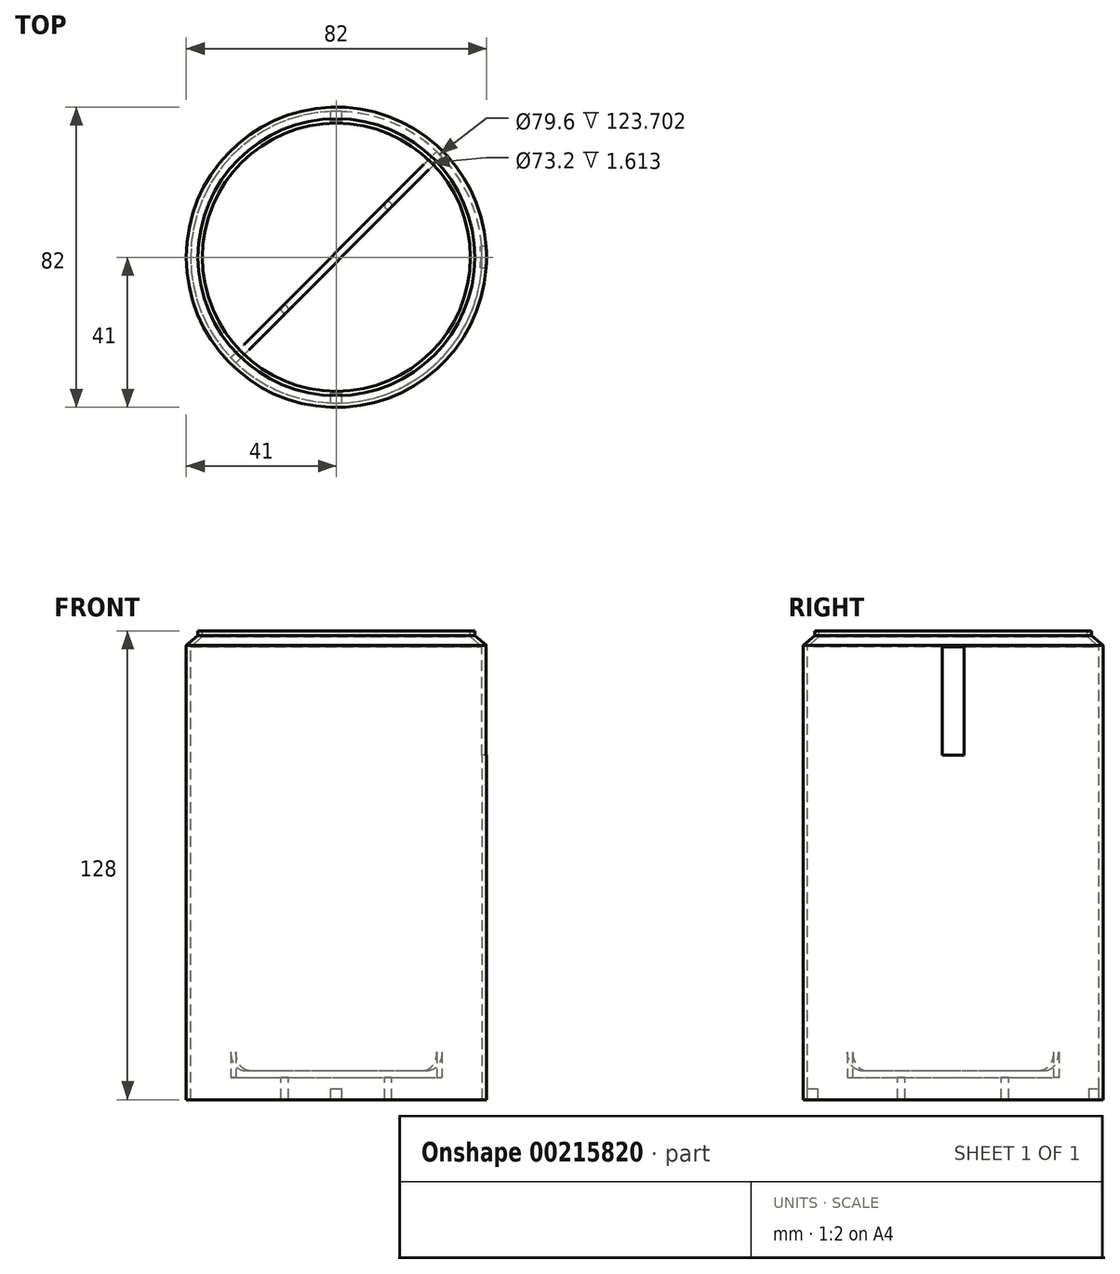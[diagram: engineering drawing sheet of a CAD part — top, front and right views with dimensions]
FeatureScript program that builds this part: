
annotation { "Feature Type Name" : "Feature", "Feature Type Description" : "" }
export const myFeature = defineFeature(function(context is Context, id is Id, definition is map)
    precondition{}
    {
        {
            var Q0;
            Q0=qCreatedBy(makeId("Right.planeOp"),FACE);
            var sketch = newSketch(context, id + "F0", { "sketchPlane" : qUnion([Q0])});
            skLineSegment(sketch, "E0", {"start": v(-41, 0) * mm, "end": v(-41, 124) * mm});
            skLineSegment(sketch, "E1", {"start": v(-39.8, 123.7) * mm, "end": v(-39.8, 0) * mm});
            skLineSegment(sketch, "E2", {"start": v(-39.8, 0) * mm, "end": v(-41, 0) * mm});
            skLineSegment(sketch, "E3", {"start": v(0, 64.87) * mm, "end": v(0, 0) * mm, "construction": true});
            skLineSegment(sketch, "E4", {"start": v(-37.8, 128) * mm, "end": v(-36.6, 128) * mm});
            skLineSegment(sketch, "E5", {"start": v(-37.8, 128) * mm, "end": v(-37.8, 126.69) * mm});
            skLineSegment(sketch, "E6", {"start": v(-36.6, 128) * mm, "end": v(-36.6, 126.39) * mm});
            skLineSegment(sketch, "E7", {"start": v(-37.8, 126.69) * mm, "end": v(-41, 124) * mm});
            skLineSegment(sketch, "E8", {"start": v(-36.6, 126.39) * mm, "end": v(-39.8, 123.7) * mm});
            skSolve(sketch);
        }
        {
            var Q0;
            Q0=qSketchRegion(id+"F0",true);
            var Q1;
            Q1=sQuery(id+"F0.wireOp",EDGE,"E3");
            revolve(context, id + "F1", {"entities" : qUnion([Q0]), "axis" : qUnion([Q1]), "revolveType" : RevolveType.FULL});
        }
        {
            var Q0;
            Q0=qCreatedBy(makeId("Right.planeOp"),FACE);
            var sketch = newSketch(context, id + "F2", { "sketchPlane" : qUnion([Q0])});
            skLineSegment(sketch, "E9.bottom", {"start": v(-3, 124) * mm, "end": v(3, 124) * mm});
            skLineSegment(sketch, "E9.top", {"start": v(-3, 94) * mm, "end": v(3, 94) * mm});
            skLineSegment(sketch, "E9.left", {"start": v(-3, 124) * mm, "end": v(-3, 94) * mm});
            skLineSegment(sketch, "E9.right", {"start": v(3, 124) * mm, "end": v(3, 94) * mm});
            skSolve(sketch);
        }
        {
            var Q0;
            Q0=qSketchRegion(id+"F2",true);
            extrude(context, id + "F3", {"entities" : qUnion([Q0]), "operationType" : NewBodyOperationType.REMOVE, "endBound" : BoundingType.THROUGH_ALL, "depth" : 25 * mm});
        }
        {
            var Q0;
            Q0=makeQuery(id+"F1.opRevolve","SWEPT_FACE",FACE,{"disambiguationData":[OSD([sQuery(id+"F0.wireOp",EDGE,"E2")])]});
            var sketch = newSketch(context, id + "F4", { "sketchPlane" : qUnion([Q0])});
            skLineSegment(sketch, "E10.bottom", {"start": v(-1.5, 40.97) * mm, "end": v(1.5, 40.97) * mm});
            skLineSegment(sketch, "E10.top", {"start": v(-1.5, -40.97) * mm, "end": v(1.5, -40.97) * mm});
            skLineSegment(sketch, "E10.left", {"start": v(-1.5, 40.97) * mm, "end": v(-1.5, -40.97) * mm});
            skLineSegment(sketch, "E10.right", {"start": v(1.5, 40.97) * mm, "end": v(1.5, -40.97) * mm});
            skSolve(sketch);
        }
        {
            var Q0;
            Q0=qSketchRegion(id+"F4",true);
            extrude(context, id + "F5", {"entities" : qUnion([Q0]), "operationType" : NewBodyOperationType.ADD, "oppositeDirection" : true, "depth" : 3 * mm});
        }
        {
            var Q0;
            {var subQ0=sQuery(id+"F4.wireOp",EDGE,"E10.right");var subQ1=sQuery(id+"F4.wireOp",EDGE,"E10.left");var subQ2=sQuery(id+"F4.wireOp",EDGE,"E10.top");var subQ3=sQuery(id+"F4.wireOp",EDGE,"E10.bottom");Q0=makeQuery(id+"Fm3hgB5jgAHXXEo_1.1.F5.boolean.opBoolean","MERGE",FACE,{"derivedFrom":[makeQuery(id+"F5.boolean.opBoolean","MERGE",FACE,{"derivedFrom":[makeQuery(id+"F1.opRevolve","SWEPT_FACE",FACE,{"disambiguationData":[OSD([sQuery(id+"F0.wireOp",EDGE,"E2")])]}),makeQuery(id+"F5.opExtrude","CAP_FACE",FACE,{"disambiguationData":[OSD([subQ3,subQ2,subQ1,subQ0])],"isStart":true})]}),makeQuery(id+"Fm3hgB5jgAHXXEo_1.1.F5.opExtrude","CAP_FACE",FACE,{"disambiguationData":[OSD([subQ3,subQ2,subQ1,subQ0])],"isStart":true})]});}
            var sketch = newSketch(context, id + "F6", { "sketchPlane" : qUnion([Q0])});
            skCircle(sketch, "E11", {"center": v(0, 0) * mm, "radius": 37 * mm});
            skSolve(sketch);
        }
        {
            var Q0;
            Q0=qSketchRegion(id+"F6",true);
            extrude(context, id + "F7", {"entities" : qUnion([Q0]), "operationType" : NewBodyOperationType.REMOVE, "oppositeDirection" : true, "depth" : 5 * mm});
        }
        {
            var Q0;
            {var subQ0=sQuery(id+"F4.wireOp",EDGE,"E10.right");var subQ1=sQuery(id+"F4.wireOp",EDGE,"E10.left");var subQ2=sQuery(id+"F4.wireOp",EDGE,"E10.top");var subQ3=sQuery(id+"F4.wireOp",EDGE,"E10.bottom");Q0=makeQuery(id+"Fm3hgB5jgAHXXEo_1.1.F5.boolean.opBoolean","MERGE",FACE,{"derivedFrom":[makeQuery(id+"F5.boolean.opBoolean","MERGE",FACE,{"derivedFrom":[makeQuery(id+"F1.opRevolve","SWEPT_FACE",FACE,{"disambiguationData":[OSD([sQuery(id+"F0.wireOp",EDGE,"E2")])]}),makeQuery(id+"F5.opExtrude","CAP_FACE",FACE,{"disambiguationData":[OSD([subQ3,subQ2,subQ1,subQ0])],"isStart":true})]}),makeQuery(id+"Fm3hgB5jgAHXXEo_1.1.F5.opExtrude","CAP_FACE",FACE,{"disambiguationData":[OSD([subQ3,subQ2,subQ1,subQ0])],"isStart":true})]});}
            cPlane(context, id + "F8", {"entities" : qUnion([Q0]), "cplaneType" : CPlaneType.OFFSET, "offset" : 6 * mm, "oppositeDirection" : true, "width" : 150 * mm, "height" : 150 * mm});
        }
        {
            var Q0;
            Q0=qCreatedBy(id+"F8.planeOp",FACE);
            var sketch = newSketch(context, id + "F9", { "sketchPlane" : qUnion([Q0])});
            skLineSegment(sketch, "E12", {"start": v(-28.84, 27.43) * mm, "end": v(27.43, -28.84) * mm});
            skLineSegment(sketch, "E13", {"start": v(-27.43, 28.84) * mm, "end": v(28.84, -27.43) * mm});
            skLineSegment(sketch, "E14", {"start": v(-27.43, 27.43) * mm, "end": v(0, 0) * mm, "construction": true});
            skArc(sketch, "E15", {"start": v(-27.43, 28.84) * mm, "mid": v(-28.34, 28.34) * mm, "end": v(-28.84, 27.43) * mm});
            skArc(sketch, "E16", {"start": v(27.43, -28.84) * mm, "mid": v(28.27, -28.27) * mm, "end": v(28.84, -27.43) * mm});
            skSolve(sketch);
        }
        {
            var Q0;
            Q0=qSketchRegion(id+"F9",true);
            extrude(context, id + "F10", {"entities" : qUnion([Q0]), "operationType" : NewBodyOperationType.ADD, "oppositeDirection" : true, "depth" : 2 * mm});
        }
        {
            var Q0;
            Q0=makeQuery(id+"F10.opExtrude","CAP_FACE",FACE,{"disambiguationData":[OSD([sQuery(id+"F9.wireOp",EDGE,"E12"),sQuery(id+"F9.wireOp",EDGE,"E13"),sQuery(id+"F9.wireOp",EDGE,"E15"),sQuery(id+"F9.wireOp",EDGE,"E16")])],"isStart":true});
            var sketch = newSketch(context, id + "F11", { "sketchPlane" : qUnion([Q0])});
            skLineSegment(sketch, "E17", {"start": v(0, 0) * mm, "end": v(11.82, 11.82) * mm, "construction": true});
            skLineSegment(sketch, "E18", {"start": v(-14.14, 14.14) * mm, "end": v(0, 0) * mm, "construction": true});
            skCircle(sketch, "E19", {"center": v(-14.14, 14.14) * mm, "radius": 1 * mm});
            skCircle(sketch, "E20.MirrorC", {"center": v(14.14, -14.14) * mm, "radius": 1 * mm});
            skSolve(sketch);
        }
        {
            var Q0;
            Q0=qSketchRegion(id+"F11",true);
            var Q1;
            {var subQ0=sQuery(id+"F4.wireOp",EDGE,"E10.right");var subQ1=sQuery(id+"F4.wireOp",EDGE,"E10.left");var subQ2=sQuery(id+"F4.wireOp",EDGE,"E10.top");var subQ3=sQuery(id+"F4.wireOp",EDGE,"E10.bottom");Q1=makeQuery(id+"Fm3hgB5jgAHXXEo_1.1.F5.boolean.opBoolean","MERGE",FACE,{"derivedFrom":[makeQuery(id+"F5.boolean.opBoolean","MERGE",FACE,{"derivedFrom":[makeQuery(id+"F1.opRevolve","SWEPT_FACE",FACE,{"disambiguationData":[OSD([sQuery(id+"F0.wireOp",EDGE,"E2")])]}),makeQuery(id+"F5.opExtrude","CAP_FACE",FACE,{"disambiguationData":[OSD([subQ3,subQ2,subQ1,subQ0])],"isStart":true})]}),makeQuery(id+"Fm3hgB5jgAHXXEo_1.1.F5.opExtrude","CAP_FACE",FACE,{"disambiguationData":[OSD([subQ3,subQ2,subQ1,subQ0])],"isStart":true})]});}
            extrude(context, id + "F12", {"entities" : qUnion([Q0]), "operationType" : NewBodyOperationType.ADD, "endBound" : BoundingType.UP_TO_SURFACE, "endBoundEntityFace" : qUnion([Q1]), "depth" : 25 * mm});
        }
        {
            var Q0;
            Q0=makeQuery(id+"F10.boolean.opBoolean","INTERSECT",EDGE,{"disambiguationData":[OD(1.0)],"derivedFrom":[makeQuery(id+"F1.opRevolve","SWEPT_FACE",FACE,{"disambiguationData":[OSD([sQuery(id+"F0.wireOp",EDGE,"E1")])]}),makeQuery(id+"F10.opExtrude","CAP_FACE",FACE,{"disambiguationData":[OSD([sQuery(id+"F9.wireOp",EDGE,"E12"),sQuery(id+"F9.wireOp",EDGE,"E13"),sQuery(id+"F9.wireOp",EDGE,"E15"),sQuery(id+"F9.wireOp",EDGE,"E16")])],"isStart":false})]});
            var Q1;
            Q1=makeQuery(id+"FqhN9CS0vOLvWld_1.1.F10.boolean.opBoolean","INTERSECT",EDGE,{"disambiguationData":[OD(1.0)],"derivedFrom":[makeQuery(id+"F1.opRevolve","SWEPT_FACE",FACE,{"disambiguationData":[OSD([sQuery(id+"F0.wireOp",EDGE,"E1")])]}),makeQuery(id+"FqhN9CS0vOLvWld_1.1.F10.opExtrude","CAP_FACE",FACE,{"disambiguationData":[OSD([sQuery(id+"F9.wireOp",EDGE,"E12"),sQuery(id+"F9.wireOp",EDGE,"E13"),sQuery(id+"F9.wireOp",EDGE,"E15"),sQuery(id+"F9.wireOp",EDGE,"E16")])],"isStart":false})]});
            var Q2;
            Q2=makeQuery(id+"F10.boolean.opBoolean","INTERSECT",EDGE,{"disambiguationData":[OD(0.0)],"derivedFrom":[makeQuery(id+"F1.opRevolve","SWEPT_FACE",FACE,{"disambiguationData":[OSD([sQuery(id+"F0.wireOp",EDGE,"E1")])]}),makeQuery(id+"F10.opExtrude","CAP_FACE",FACE,{"disambiguationData":[OSD([sQuery(id+"F9.wireOp",EDGE,"E12"),sQuery(id+"F9.wireOp",EDGE,"E13"),sQuery(id+"F9.wireOp",EDGE,"E15"),sQuery(id+"F9.wireOp",EDGE,"E16")])],"isStart":false})]});
            var Q3;
            Q3=makeQuery(id+"FqhN9CS0vOLvWld_1.1.F10.boolean.opBoolean","INTERSECT",EDGE,{"disambiguationData":[OD(0.0)],"derivedFrom":[makeQuery(id+"F1.opRevolve","SWEPT_FACE",FACE,{"disambiguationData":[OSD([sQuery(id+"F0.wireOp",EDGE,"E1")])]}),makeQuery(id+"FqhN9CS0vOLvWld_1.1.F10.opExtrude","CAP_FACE",FACE,{"disambiguationData":[OSD([sQuery(id+"F9.wireOp",EDGE,"E12"),sQuery(id+"F9.wireOp",EDGE,"E13"),sQuery(id+"F9.wireOp",EDGE,"E15"),sQuery(id+"F9.wireOp",EDGE,"E16")])],"isStart":false})]});
            fillet(context, id + "F13", {"entities" : qUnion([Q0, Q1, Q2, Q3]), "radius" : 5 * mm, "tangentPropagation" : true, "allowEdgeOverflow" : false});
        }
    });
